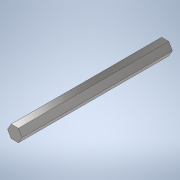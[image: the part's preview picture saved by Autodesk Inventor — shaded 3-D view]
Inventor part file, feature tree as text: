
AUTODESK INVENTOR PART (.ipt)
format: ipt  version: 2020 (Build 240168000, 168)  size: 100,352 bytes
history: native  units: in
note: dims shown in document units (in); Inventor stores cm internally (conversion verified against a paired STEP export)
features: extrude x1, sketch x1
ambient origin geometry x8: Origin, YZ Plane, XZ Plane, XY Plane, X Axis, Y Axis, Z Axis, Center Point
bodies: Solid1 (feature_tree)
feature tree (2):
  extrude  "Extrusion1"  Depth=6.0in TaperAngle=0.0deg
  sketch  "Sketch1"  dims[d0=0.5in d1=6.0in d2=0.0in]
